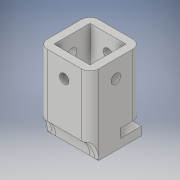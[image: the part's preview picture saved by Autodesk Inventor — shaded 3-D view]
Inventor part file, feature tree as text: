
AUTODESK INVENTOR PART (.ipt)
format: ipt  version: 2019.4 (Build 234330000, 330)  size: 217,088 bytes
history: native  units: mm
features: extrude x7, sketch x7, fillet x2
ambient origin geometry x8: Origin, YZ Plane, XZ Plane, XY Plane, X Axis, Y Axis, Z Axis, Center Point
bodies: Solid1 (feature_tree)
feature tree (16):
  extrude  "Extrusion1"  Depth=30.0mm
  extrude  "Extrusion2"  Depth=4.5mm
  extrude  "Extrusion3"  Depth=21.0mm
  fillet  "Fillet2"  Radius=21.0mm
  extrude  "Extrusion4"  Depth=15.0mm
  extrude  "Extrusion5"  Depth=5.0mm TaperAngle=0.0deg
  fillet  "Fillet3"  Radius=5.0mm
  extrude  "Extrusion6"  Depth=10.0mm
  extrude  "Extrusion7"  TaperAngle=60.0deg  [1 undecoded]
  sketch  "Sketch1"  dims[d0=30.0mm d1=30.0mm]
  sketch  "Sketch2"  dims[d2=36.35mm d3=0.0mm d4=4.5mm]
  sketch  "Sketch3"  dims[d5=4.5mm d6=21.0mm d7=21.0mm]
  sketch  "Sketch4"  dims[d8=30.0mm d9=0.0mm d10=15.0mm]
  sketch  "Sketch5"  dims[d11=4.0mm d12=5.0mm d13=0.0mm d15=5.0mm]
  sketch  "Sketch6"  dims[d16=10.0mm d17=6.0mm]
  sketch  "Sketch7"  dims[d18=90.0deg d19=60.0deg d20=5.0mm d21=0.0mm d22=30.0mm d23=25.0mm d24=5.0mm d25=0.0mm d26=13.0mm d27=10.0mm d28=90.0deg d29=5.5mm d30=30.0mm d31=0.0mm d32=10.0mm d33=90.0deg d34=5.5mm d35=30.0mm d36=0.0mm]
note: 1 required parameter value undecoded (feature->parameter linkage not recoverable at this tier; creation-order binding heuristic only, values carry confidence <= 0.55)
